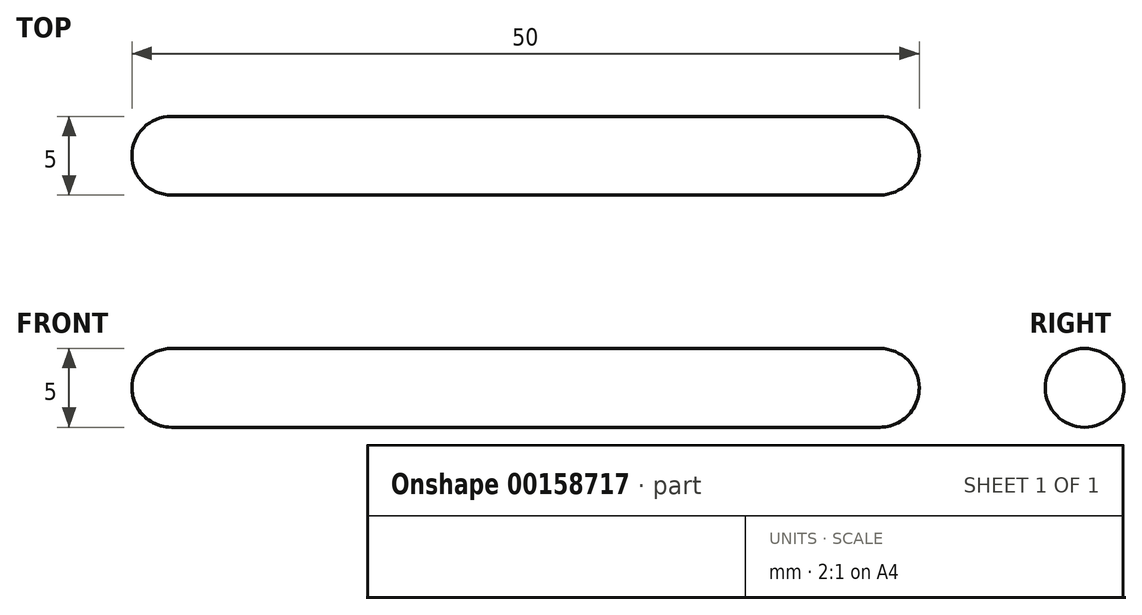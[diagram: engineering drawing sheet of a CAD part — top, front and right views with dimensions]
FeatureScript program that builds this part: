
annotation { "Feature Type Name" : "Feature", "Feature Type Description" : "" }
export const myFeature = defineFeature(function(context is Context, id is Id, definition is map)
    precondition{}
    {
        {
            var Q0;
            Q0=qCreatedBy(makeId("Right.planeOp"),FACE);
            var sketch = newSketch(context, id + "F0", { "sketchPlane" : qUnion([Q0])});
            skCircle(sketch, "E0", {"center": v(0, 0) * mm, "radius": 2.5 * mm});
            skSolve(sketch);
        }
        {
            var Q0;
            Q0 = qSketchRegion(id + "F0", true);
            extrude(context, id + "F1", {"entities" : qUnion([Q0]), "depth" : 50 * mm});
        }
        {
            var Q0;
            Q0=makeQuery(id+"F1.opExtrude","CAP_EDGE",EDGE,{"disambiguationData":[OSD([sQuery(id+"F0.wireOp",EDGE,"E0")])],"isStart":false});
            fillet(context, id + "F2", {"entities" : qUnion([Q0]), "radius" : 2.5 * mm, "tangentPropagation" : true, "allowEdgeOverflow" : false});
        }
        {
            var Q0;
            Q0=makeQuery(id+"F1.opExtrude","CAP_EDGE",EDGE,{"disambiguationData":[OSD([sQuery(id+"F0.wireOp",EDGE,"E0")])],"isStart":true});
            fillet(context, id + "F3", {"entities" : qUnion([Q0]), "radius" : 2.5 * mm, "tangentPropagation" : true, "allowEdgeOverflow" : false});
        }
    });
